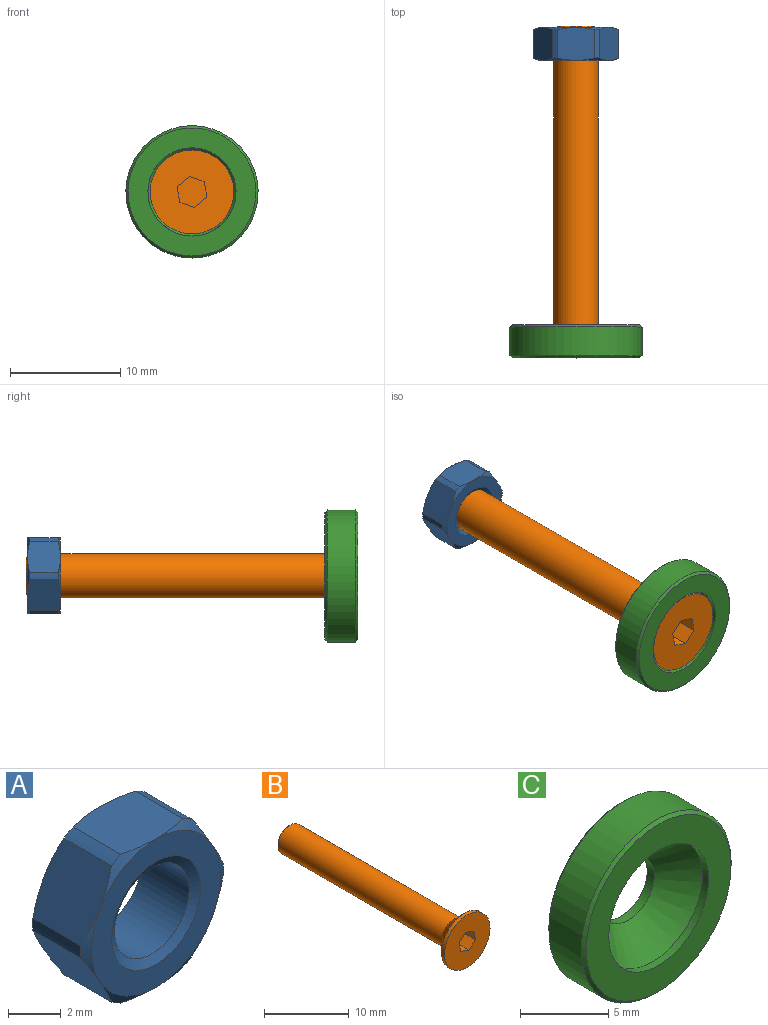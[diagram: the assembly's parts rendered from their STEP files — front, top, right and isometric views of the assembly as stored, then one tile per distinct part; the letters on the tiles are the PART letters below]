
ASSEMBLY  parts=3 mates=2
PART A: 19 faces, bbox 7.7x3x7.7 mm
  f0: cylinder r=3.83mm len=2.56mm, axis (0,-1,0), area 1.5mm2, adj f11,f12,f17,f18
  f1: cylinder r=3.83mm len=2.56mm, axis (0,-1,0), area 1.5mm2, adj f11,f12,f16,f17
  f2: cylinder r=3.83mm len=2.56mm, axis (0,-1,0), area 1.5mm2, adj f11,f12,f15,f16
  f3: cylinder r=3.83mm len=2.56mm, axis (0,-1,0), area 1.5mm2, adj f11,f12,f14,f15
  f4: cylinder r=3.83mm len=2.56mm, axis (0,-1,0), area 1.5mm2, adj f11,f12,f13,f14
  f5: cylinder r=2mm len=4mm, axis (0,-1,0), area 32.1mm2, adj f9,f10
  f6: plane 6.89x6.89mm, normal (0,1,0), area 19.4mm2, adj f9,f11
  f7: cylinder r=3.83mm len=2.56mm, axis (0,-1,0), area 1.5mm2, adj f11,f12,f13,f18
  f8: plane 6.89x6.89mm, normal (0,-1,0), area 19.4mm2, adj f10,f12
  f9: cone r=2.38mm half-angle=60deg, axis (0,1,0), area 6.1mm2, adj f5,f6
  f10: cone r=2mm half-angle=60deg, axis (0,-1,0), area 6.1mm2, adj f5,f8
  f11: cone r=3.83mm half-angle=60deg, axis (0,-1,0), area 4.3mm2, adj f0,f1,f2,f3,f4,f6,f7,f13
  f12: cone r=3.45mm half-angle=60deg, axis (0,1,0), area 4.3mm2, adj f0,f1,f2,f3,f4,f7,f8,f13
  f13: plane 3x2.88mm, normal (-0.87,0,0.5), area 9.5mm2, adj f4,f7,f11,f12
  f14: plane 3x2.88mm, normal (-0.87,0,-0.5), area 9.5mm2, adj f3,f4,f11,f12
  f15: plane 3.33x3mm, normal (0,0,-1), area 9.5mm2, adj f2,f3,f11,f12
  f16: plane 3x2.88mm, normal (0.87,0,-0.5), area 9.5mm2, adj f1,f2,f11,f12
  f17: plane 3x2.88mm, normal (0.87,0,0.5), area 9.5mm2, adj f0,f1,f11,f12
  f18: plane 3.33x3mm, normal (0,0,1), area 9.5mm2, adj f0,f7,f11,f12
PART B: 13 faces, bbox 7.6x30x7.6 mm
  f0: plane 7.6x7.6mm, normal (0,-1,0), area 40mm2, adj f5,f6,f7,f8,f9,f10,f11
  f1: plane 3.29x3.29mm, normal (0,1,0), area 8.5mm2, adj f2
  f2: cone r=2mm half-angle=45deg, axis (0,-1,0), area 5.7mm2, adj f1,f3
  f3: cylinder r=2mm len=27.35mm, axis (0,1,0), area 343.6mm2, adj f2,f4
  f4: cone r=3.8mm half-angle=45deg, axis (0,-1,0), area 46.4mm2, adj f3,f5
  f5: cylinder r=3.8mm len=7.6mm, axis (0,1,0), area 11.9mm2, adj f0,f4
  f6: plane 1.8x1.1mm, normal (0.65,0,-0.76), area 2.6mm2, adj f0,f7,f11,f12
  f7: plane 1.8x1.42mm, normal (0.98,0,0.18), area 2.6mm2, adj f0,f6,f8,f12
  f8: plane 1.8x1.36mm, normal (0.33,0,0.94), area 2.6mm2, adj f0,f7,f9,f12
  f9: plane 1.8x1.1mm, normal (-0.65,0,0.76), area 2.6mm2, adj f0,f8,f10,f12
  f10: plane 1.8x1.42mm, normal (-0.98,0,-0.18), area 2.6mm2, adj f0,f9,f11,f12
  f11: plane 1.8x1.36mm, normal (-0.33,0,-0.94), area 2.6mm2, adj f0,f6,f10,f12
  f12: plane 2.84x2.72mm, normal (0,-1,0), area 5.4mm2, adj f6,f7,f8,f9,f10,f11
PART C: 8 faces, bbox 12x3x12 mm
  f0: cylinder r=2.08mm len=4.15mm, axis (0,1,0), area 7.5mm2, adj f3,f4
  f1: cylinder r=6mm len=12mm, axis (0,1,0), area 98mm2, adj f6,f7
  f2: plane 11.6x11.6mm, normal (0,-1,0), area 55.4mm2, adj f5,f7
  f3: plane 11.6x11.6mm, normal (0,1,0), area 92.2mm2, adj f0,f6
  f4: cone r=4mm half-angle=45deg, axis (0,-1,0), area 52mm2, adj f0,f5
  f5: cylinder r=4mm len=8mm, axis (0,-1,0), area 12.6mm2, adj f2,f4
  f6: cone r=6mm half-angle=45deg, axis (0,-1,0), area 10.5mm2, adj f1,f3
  f7: cone r=5.8mm half-angle=45deg, axis (0,1,0), area 10.5mm2, adj f1,f2
PLACE A t=(85.82,321.93,-110.43)mm
PLACE B t=(-7.19,306.48,-110.43)mm
PLACE C t=(100.49,295.43,-98.48)mm
MATE fastened B.f2 <-> C.f0  axis (0,1,0) through (85.82,297.36,-110.43)mm
MATE fastened A.f0 <-> C.f0  axis (0,-1,0) through (85.82,321.93,-110.43)mm
